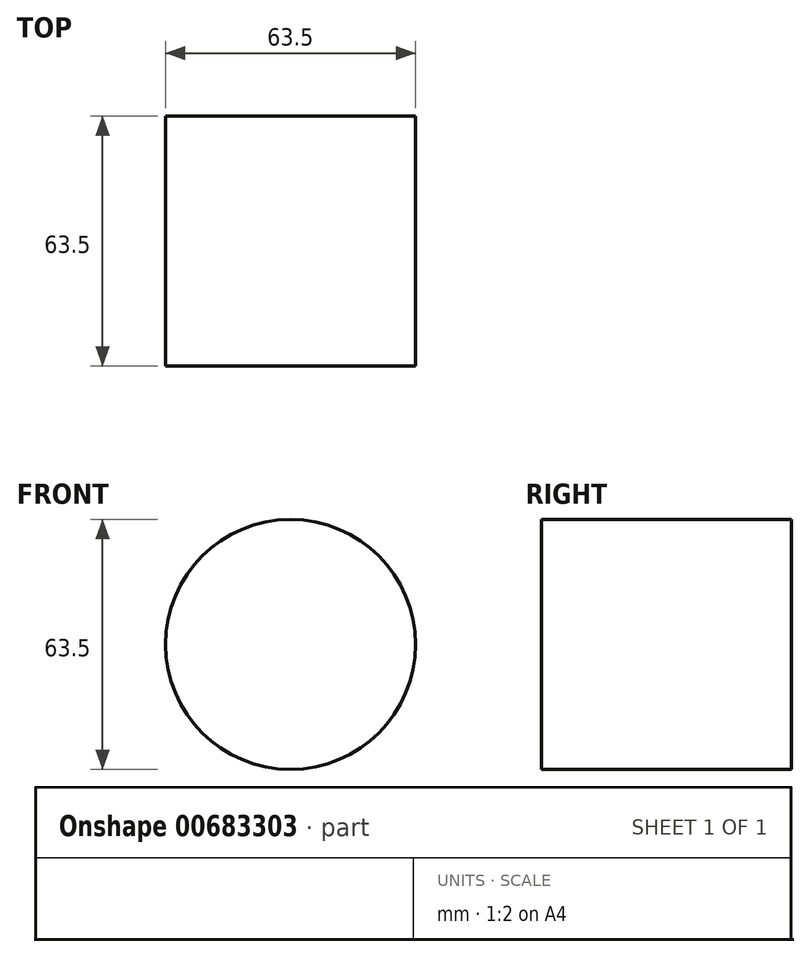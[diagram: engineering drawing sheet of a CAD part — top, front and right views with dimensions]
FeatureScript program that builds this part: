
annotation { "Feature Type Name" : "Feature", "Feature Type Description" : "" }
export const myFeature = defineFeature(function(context is Context, id is Id, definition is map)
    precondition{}
    {
        {
            var Q0;
            Q0=qCreatedBy(makeId("Front.planeOp"),FACE);
            var sketch = newSketch(context, id + "F0", { "sketchPlane" : qUnion([Q0])});
            skCircle(sketch, "E0", {"center": v(0, 0) * mm, "radius": 31.75 * mm});
            skSolve(sketch);
        }
        {
            var Q0;
            Q0 = qSketchRegion(id + "F0", true);
            extrude(context, id + "F1", {"entities" : qUnion([Q0]), "depth" : 63.5 * mm, "offsetDistance" : 25.4 * mm});
        }
    });
